# Revit family: agtatec_Record_RlvngDrsetSym_K41_Standalone
name_source: partatom
category: Doors
revit_build: Autodesk Revit Architecture 2012 (Build: 20110916_2132(x64)
units: mm (PartAtom-declared; Revit-internal decimal feet)

## types (2) — shared parameters
AccessoryOptions = Contact manufacturer
AlternativeDoorsetGlazing = Part of glazing spec
AntiFingerTrapRequirement = Yes
BIMObjectName = agtatec_Record_RevolvingDoorsetSystem_K41_Standalone
BottomConstruction = agtatec_Record_Revolving Door, Stainless Steel
CanopyCovering = agtatec_Record_Revolving Door, Sheet metal (Painted Steel)
CanopyHeight = 570.00 mm
CanopyHeightOptions = 250 mm +
CanopyRadius = 1300.00 mm
Capacity = <>
Colour = Customer specific
Configuration = 2, 3 or 4 leafs
Construction Type = Automatic Revolving Door
DepthOfRecessFloorFrame = 80.00 mm
Description = 4-wing Revolving Door
DiameterOptions = Internal 2000-4000 mm
DoorIncluded = Yes
DoorSeal = 1
DoorWingOptions = 4 wings
DoorsetFasteners = Screws
DoorsetOperation = Automatic
DrumWallPanelFill = agtatec_Record_Revolving Door, Laminated Safety Glass (Clear)
DurationUnit = year
ElectronicLock = Yes
ExternalDimensionOfFloorFrame = 2794.00 mm
Finish = Powder coated, Anodized, customer specific
FireExit = No
Floor Frame (Ring) = Yes
Flooring = agtatec_Record_Revolving Door, Felt Carpet
FrameMaterial = Aluminium
FrameProfile = Aluminium
FrameSeal = Yes
Function = Exterior
GlassThickness1 = 0.00 mm
GlassThickness2 = 0.00 mm
GlassType = Part of glazing spec
HandicapAccessible = No
Handles = Yes
HasDrive = Yes
Height = 2770.00 mm
HeightOfFloorFrame = 65.00 mm
HeightUnderCanopyOptions = Passage height: 2000 - 3000 mm
IfcExportAs = IfcExportAs
IfcExportType = Door
InnerRadius = 1271.00 mm
InsideDiameter = 2542.00 mm
IsExternal = Yes
IssueDate = <>
LeafColourOptions = All RAL, customer specific
LeafPanelFill = agtatec_Record_Revolving Door, Laminated Safety Glass (Clear)
LeafRotationAngle = 45.00°
ManufacturerName = Record
ManufacturerURL = www.agta-record.com
Material = Aluminium
Model = K41
ModelReference = Depends on the configuration
NBSDescription = Revolving Doorset System
NBSReference = 25-50-20/170
Name = RlvngDrsetSym_K41_Standalone_Record
NightShutterPanelFill = agtatec_Record_Revolving Door, Laminated Safety Glass (Clear)
NightShuttersOpen = Yes
NightShuttersOpeningAngle = 43.50°
NightShuttersRadius = 1348.50 mm
NominalHeight = 2770.00 mm
NominalLength = 2600.00 mm
NominalWidth = 2600.00 mm
OperatingTemperature = -15º to +50ºC
OuterRadius = 1297.00 mm
OutsideDiameter = 2594.00 mm
PanelFill = agtatec_Record_Revolving Door, Laminated Safety Glass (Clear)
PanelFrames = agtatec_Record_Revolving Door, Aluminium
PanelHeight = 2163.00 mm
PanelWidth = 1216.20 mm
PassageHeight = 2200.00 mm
PassageWidth = 1170.00 mm
ProductInformation = www.agta-record.com
RecessHeight = 2820.00 mm
RecessWidth = 2700.00 mm
ReferenceStandard = EN16005, EN16361, DIN 18650, etc.
ReplacementCost = Depends on the configuration and door type
Rough Height = 2776.00 mm
Rough Width = 2606.00 mm
SafetyDevices = Fully compliant with EN16005, Safety buffers, Presence sensors, etc.
SelfClosing = Yes
ServiceLifeDuration = 10-15 years
Shape = Cylinder shaped
ShowcaseRadius = 1195.00 mm
SmokeStop = No
ThresholdRequired = Yes
ThresholdStripping = No additional required, part of the doorset
TotalDiameter = 2600.00 mm
TotalHeight = 2770.00 mm
Uniclass2 = Ss_25_30_20_70
Version = Version 1.0
WarrantyDescription = Depends on country
WarrantyDurationLabour = Depends on country
WarrantyDurationParts = Depends on country
WarrantyDurationUnit = Depends on country
WarrantyGuarantorLabour = Local door manufacturer
WarrantyGuarantorParts = Local door manufacturer
Weight = Depends on configuration and size
Width = 2619.00 mm
WithinStandardSizes = Yes
zero-valued in all types: Cost, GlassLayers, ThermalTransmittance

## type names (no varying parameters)
- Default
- default

## geometry (parser evidence)
native form markers: Blend x4, Sweep x9
no freeform markers — native parametric forms only
